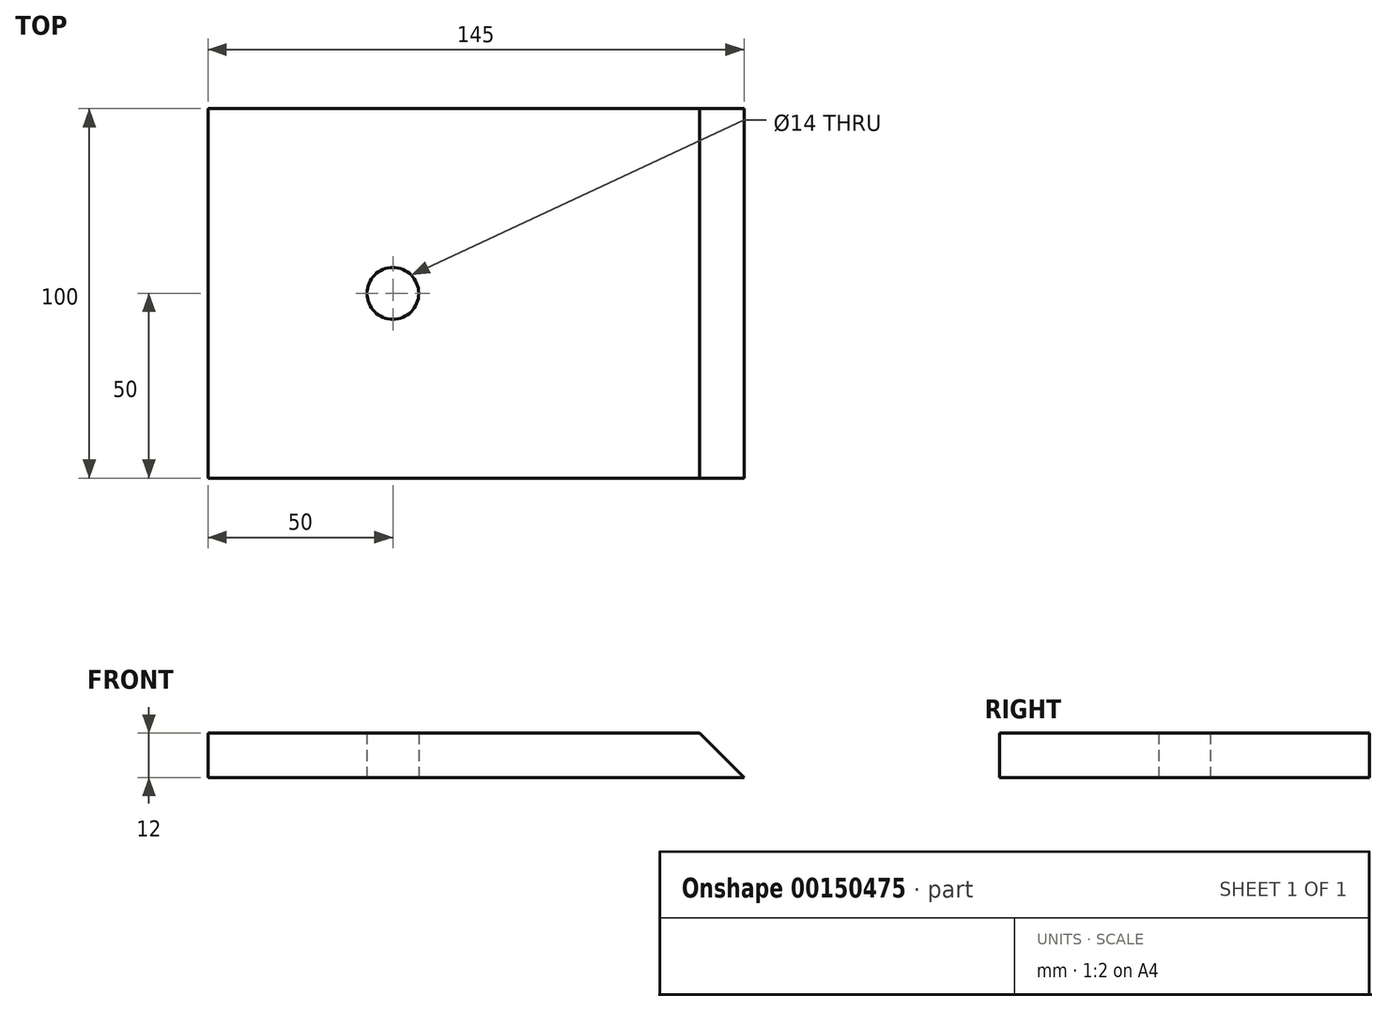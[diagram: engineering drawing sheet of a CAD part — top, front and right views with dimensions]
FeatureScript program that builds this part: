
annotation { "Feature Type Name" : "Feature", "Feature Type Description" : "" }
export const myFeature = defineFeature(function(context is Context, id is Id, definition is map)
    precondition{}
    {
        {
            var Q0;
            Q0=qCreatedBy(makeId("Front.planeOp"),FACE);
            var sketch = newSketch(context, id + "F0", { "sketchPlane" : qUnion([Q0])});
            skLineSegment(sketch, "E0.bottom", {"start": v(0, 0) * mm, "end": v(145, 0) * mm});
            skLineSegment(sketch, "E0.top", {"start": v(0, 12) * mm, "end": v(133, 12) * mm});
            skLineSegment(sketch, "E0.left", {"start": v(0, 0) * mm, "end": v(0, 12) * mm});
            skLineSegment(sketch, "E1", {"start": v(145, 0) * mm, "end": v(133, 12) * mm});
            skSolve(sketch);
        }
        {
            var Q0;
            Q0=makeQuery(id+"F0.imprint","IMPRINT",FACE,{"disambiguationData":[TD([[makeQuery(id+"F0.imprint","IMPRINT",EDGE,{"derivedFrom":sQuery(id+"F0.wireOp",EDGE,"E0.bottom")}),1.0]])]});
            extrude(context, id + "F1", {"entities" : qUnion([Q0]), "depth" : 100 * mm});
        }
        {
            var Q0;
            Q0=qCreatedBy(makeId("Top.planeOp"),FACE);
            var sketch = newSketch(context, id + "F2", { "sketchPlane" : qUnion([Q0])});
            skCircle(sketch, "E2", {"center": v(50, -50) * mm, "radius": 7 * mm});
            skSolve(sketch);
        }
        {
            var Q0;
            Q0 = qSketchRegion(id + "F2", true);
            extrude(context, id + "F3", {"entities" : qUnion([Q0]), "operationType" : NewBodyOperationType.REMOVE, "endBound" : BoundingType.THROUGH_ALL, "depth" : 25 * mm});
        }
    });
